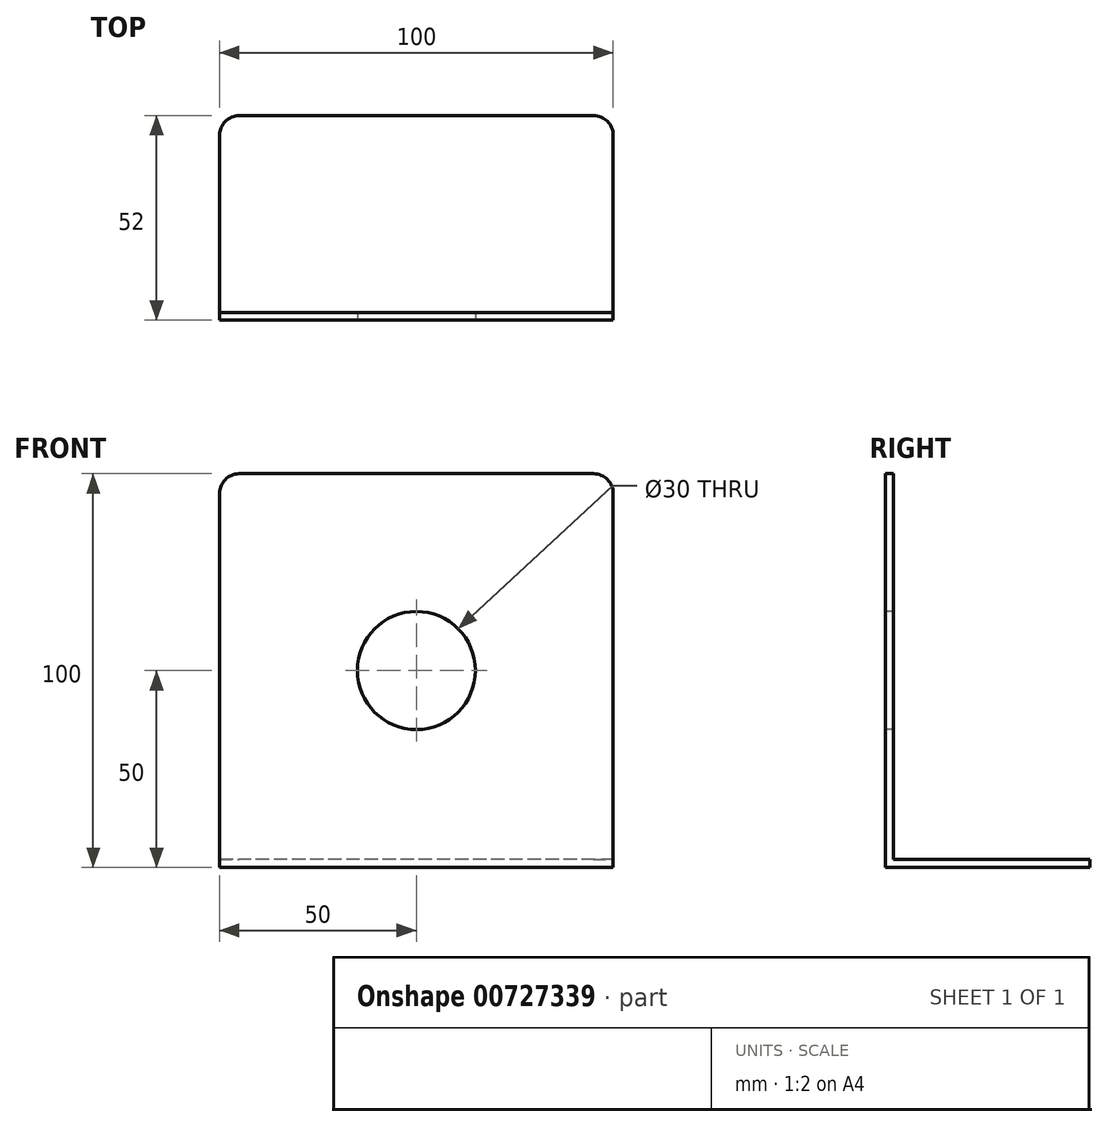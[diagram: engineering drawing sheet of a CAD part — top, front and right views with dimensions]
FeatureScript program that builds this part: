
annotation { "Feature Type Name" : "Feature", "Feature Type Description" : "" }
export const myFeature = defineFeature(function(context is Context, id is Id, definition is map)
    precondition{}
    {
        {
            var Q0;
            Q0=qCreatedBy(makeId("Front.planeOp"),FACE);
            var sketch = newSketch(context, id + "F0", { "sketchPlane" : qUnion([Q0])});
            skLineSegment(sketch, "E0.bottom", {"start": v(50, -50) * mm, "end": v(-50, -50) * mm});
            skLineSegment(sketch, "E0.top", {"start": v(50, 50) * mm, "end": v(-50, 50) * mm});
            skLineSegment(sketch, "E0.left", {"start": v(50, -50) * mm, "end": v(50, 50) * mm});
            skLineSegment(sketch, "E0.right", {"start": v(-50, -50) * mm, "end": v(-50, 50) * mm});
            skPoint(sketch, "E0.middle", {"position": v(0, 0) * mm});
            skSolve(sketch);
        }
        {
            var Q0;
            Q0 = qSketchRegion(id + "F0", true);
            extrude(context, id + "F1", {"entities" : qUnion([Q0]), "depth" : 2 * mm, "offsetDistance" : 25 * mm});
        }
        {
            var Q0;
            Q0=makeQuery(id+"F1.opExtrude","CAP_FACE",FACE,{"disambiguationData":[OSD([sQuery(id+"F0.wireOp",EDGE,"E0.bottom"),sQuery(id+"F0.wireOp",EDGE,"E0.top"),sQuery(id+"F0.wireOp",EDGE,"E0.left"),sQuery(id+"F0.wireOp",EDGE,"E0.right")])],"isStart":false});
            var sketch = newSketch(context, id + "F2", { "sketchPlane" : qUnion([Q0])});
            skCircle(sketch, "E1", {"center": v(0, 0) * mm, "radius": 15 * mm});
            skSolve(sketch);
        }
        {
            var Q0;
            Q0 = qSketchRegion(id + "F2", true);
            var Q1;
            Q1=makeQuery(id+"F1.opExtrude","CAP_FACE",FACE,{"disambiguationData":[OSD([sQuery(id+"F0.wireOp",EDGE,"E0.bottom"),sQuery(id+"F0.wireOp",EDGE,"E0.top"),sQuery(id+"F0.wireOp",EDGE,"E0.left"),sQuery(id+"F0.wireOp",EDGE,"E0.right")])],"isStart":true});
            extrude(context, id + "F3", {"entities" : qUnion([Q0]), "operationType" : NewBodyOperationType.REMOVE, "oppositeDirection" : true, "depth" : 25 * mm, "endBoundEntityFace" : qUnion([Q1]), "offsetDistance" : 25 * mm});
        }
        {
            var Q0;
            Q0=makeQuery(id+"F1.opExtrude","SWEPT_FACE",FACE,{"disambiguationData":[OSD([sQuery(id+"F0.wireOp",EDGE,"E0.bottom")])]});
            var sketch = newSketch(context, id + "F4", { "sketchPlane" : qUnion([Q0])});
            skLineSegment(sketch, "E2.bottom", {"start": v(50, 0) * mm, "end": v(-50, 0) * mm});
            skLineSegment(sketch, "E2.top", {"start": v(50, -50) * mm, "end": v(-50, -50) * mm});
            skLineSegment(sketch, "E2.left", {"start": v(50, 0) * mm, "end": v(50, -50) * mm});
            skLineSegment(sketch, "E2.right", {"start": v(-50, 0) * mm, "end": v(-50, -50) * mm});
            skSolve(sketch);
        }
        {
            var Q0;
            Q0 = qSketchRegion(id + "F4", true);
            extrude(context, id + "F5", {"entities" : qUnion([Q0]), "operationType" : NewBodyOperationType.ADD, "oppositeDirection" : true, "depth" : 2 * mm, "offsetDistance" : 25 * mm});
        }
        {
            var Q0;
            Q0=makeQuery(id+"F1.opExtrude","SWEPT_EDGE",EDGE,{"disambiguationData":[OSD([sQuery(id+"F0.wireOp",EDGE,"E0.top"),sQuery(id+"F0.wireOp",EDGE,"E0.left")])]});
            var Q1;
            Q1=makeQuery(id+"F5.opExtrude","SWEPT_EDGE",EDGE,{"disambiguationData":[OSD([sQuery(id+"F4.wireOp",EDGE,"E2.top"),sQuery(id+"F4.wireOp",EDGE,"E2.left")])]});
            var Q2;
            Q2=makeQuery(id+"F5.opExtrude","SWEPT_EDGE",EDGE,{"disambiguationData":[OSD([sQuery(id+"F4.wireOp",EDGE,"E2.top"),sQuery(id+"F4.wireOp",EDGE,"E2.right")])]});
            var Q3;
            Q3=makeQuery(id+"F1.opExtrude","SWEPT_EDGE",EDGE,{"disambiguationData":[OSD([sQuery(id+"F0.wireOp",EDGE,"E0.top"),sQuery(id+"F0.wireOp",EDGE,"E0.right")])]});
            fillet(context, id + "F6", {"entities" : qUnion([Q0, Q1, Q2, Q3]), "radius" : 5 * mm, "tangentPropagation" : true, "allowEdgeOverflow" : false});
        }
    });
